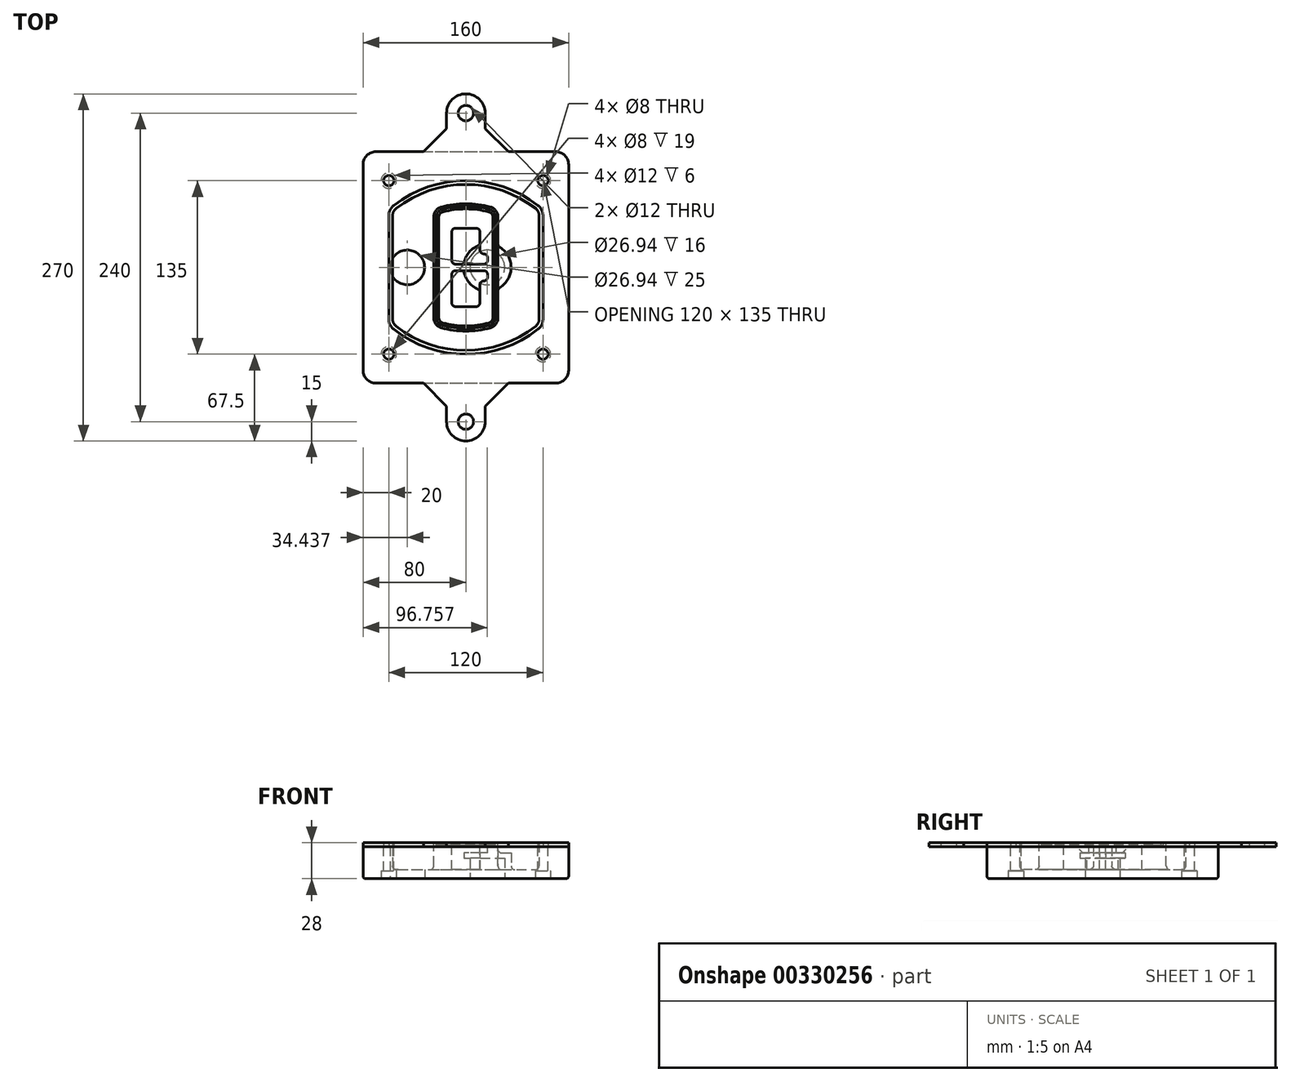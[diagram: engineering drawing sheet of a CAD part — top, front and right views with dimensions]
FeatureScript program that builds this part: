
annotation { "Feature Type Name" : "Feature", "Feature Type Description" : "" }
export const myFeature = defineFeature(function(context is Context, id is Id, definition is map)
    precondition{}
    {
        {
            var Q0;
            Q0=qCreatedBy(makeId("Top.planeOp"),FACE);
            var sketch = newSketch(context, id + "F0", { "sketchPlane" : qUnion([Q0])});
            skPoint(sketch, "E0.rect.middle", {"position": v(0, 0) * mm});
            skLineSegment(sketch, "E1.bottom", {"start": v(-70, -90) * mm, "end": v(70, -90) * mm});
            skLineSegment(sketch, "E1.top", {"start": v(-70, 90) * mm, "end": v(70, 90) * mm});
            skLineSegment(sketch, "E1.left", {"start": v(-80, -80) * mm, "end": v(-80, 80) * mm});
            skLineSegment(sketch, "E1.right", {"start": v(80, -80) * mm, "end": v(80, 80) * mm});
            skLineSegment(sketch, "E2", {"start": v(-80, 90) * mm, "end": v(80, -90) * mm, "construction": true});
            skLineSegment(sketch, "E3", {"start": v(80, 90) * mm, "end": v(-80, -90) * mm, "construction": true});
            skCircle(sketch, "E4", {"center": v(-60, 67.5) * mm, "radius": 4 * mm});
            skCircle(sketch, "E5", {"center": v(60, 67.5) * mm, "radius": 4 * mm});
            skCircle(sketch, "E6", {"center": v(60, -67.5) * mm, "radius": 4 * mm});
            skCircle(sketch, "E7", {"center": v(-60, -67.5) * mm, "radius": 4 * mm});
            skLineSegment(sketch, "E8", {"start": v(-60, 67.5) * mm, "end": v(60, 67.5) * mm, "construction": true});
            skLineSegment(sketch, "E9", {"start": v(60, 67.5) * mm, "end": v(60, -67.5) * mm, "construction": true});
            skLineSegment(sketch, "E10", {"start": v(60, -67.5) * mm, "end": v(-60, -67.5) * mm, "construction": true});
            skLineSegment(sketch, "E11", {"start": v(-60, -67.5) * mm, "end": v(-60, 67.5) * mm, "construction": true});
            skLineSegment(sketch, "E12", {"start": v(-60, 40.3) * mm, "end": v(-60, -40.3) * mm});
            skLineSegment(sketch, "E13", {"start": v(60, 40.3) * mm, "end": v(60, -40.3) * mm});
            skArc(sketch, "E14", {"start": v(56.15, 48.18) * mm, "mid": v(0, 67.5) * mm, "end": v(-56.15, 48.18) * mm});
            skArc(sketch, "E15", {"start": v(-56.15, -48.18) * mm, "mid": v(0, -67.5) * mm, "end": v(56.15, -48.18) * mm});
            skLineSegment(sketch, "E16", {"start": v(-60, 0) * mm, "end": v(60, 0) * mm, "construction": true});
            skPoint(sketch, "E17.visualSharp", {"position": v(-60, -45) * mm});
            skArc(sketch, "E17.filletArc", {"start": v(-60, -40.3) * mm, "mid": v(-58.99, -44.68) * mm, "end": v(-56.15, -48.18) * mm});
            skPoint(sketch, "E18.visualSharp", {"position": v(-60, 45) * mm});
            skArc(sketch, "E18.filletArc", {"start": v(-56.15, 48.18) * mm, "mid": v(-58.99, 44.68) * mm, "end": v(-60, 40.3) * mm});
            skPoint(sketch, "E19.visualSharp", {"position": v(60, 45) * mm});
            skArc(sketch, "E19.filletArc", {"start": v(60, 40.3) * mm, "mid": v(58.99, 44.68) * mm, "end": v(56.15, 48.18) * mm});
            skPoint(sketch, "E20.visualSharp", {"position": v(60, -45) * mm});
            skArc(sketch, "E20.filletArc", {"start": v(56.15, -48.18) * mm, "mid": v(58.99, -44.68) * mm, "end": v(60, -40.3) * mm});
            skPoint(sketch, "E21.visualSharp", {"position": v(-80, 90) * mm});
            skArc(sketch, "E21.filletArc", {"start": v(-70, 90) * mm, "mid": v(-77.07, 87.07) * mm, "end": v(-80, 80) * mm});
            skPoint(sketch, "E22.visualSharp", {"position": v(80, 90) * mm});
            skArc(sketch, "E22.filletArc", {"start": v(80, 80) * mm, "mid": v(77.07, 87.07) * mm, "end": v(70, 90) * mm});
            skPoint(sketch, "E23.visualSharp", {"position": v(80, -90) * mm});
            skArc(sketch, "E23.filletArc", {"start": v(70, -90) * mm, "mid": v(77.07, -87.07) * mm, "end": v(80, -80) * mm});
            skPoint(sketch, "E24.visualSharp", {"position": v(-80, -90) * mm});
            skArc(sketch, "E24.filletArc", {"start": v(-80, -80) * mm, "mid": v(-77.07, -87.07) * mm, "end": v(-70, -90) * mm});
            skArc(sketch, "E25.0", {"start": v(57, 40.3) * mm, "mid": v(56.3, 43.36) * mm, "end": v(54.3, 45.81) * mm});
            skLineSegment(sketch, "E25.1", {"start": v(57, 40.3) * mm, "end": v(57, -40.3) * mm});
            skArc(sketch, "E25.2", {"start": v(54.3, -45.81) * mm, "mid": v(56.3, -43.36) * mm, "end": v(57, -40.3) * mm});
            skArc(sketch, "E25.3", {"start": v(-54.3, -45.81) * mm, "mid": v(0, -64.5) * mm, "end": v(54.3, -45.81) * mm});
            skArc(sketch, "E25.4", {"start": v(-57, -40.3) * mm, "mid": v(-56.3, -43.36) * mm, "end": v(-54.3, -45.81) * mm});
            skArc(sketch, "E25.5", {"start": v(54.3, 45.81) * mm, "mid": v(0, 64.5) * mm, "end": v(-54.3, 45.81) * mm});
            skLineSegment(sketch, "E25.6", {"start": v(-57, 40.3) * mm, "end": v(-57, -40.3) * mm});
            skArc(sketch, "E25.7", {"start": v(-54.3, 45.81) * mm, "mid": v(-56.3, 43.36) * mm, "end": v(-57, 40.3) * mm});
            skArc(sketch, "E26.0", {"start": v(-58.62, 51.33) * mm, "mid": v(-62.58, 46.43) * mm, "end": v(-64, 40.3) * mm});
            skArc(sketch, "E26.1", {"start": v(58.62, 51.33) * mm, "mid": v(0, 71.5) * mm, "end": v(-58.62, 51.33) * mm});
            skArc(sketch, "E26.2", {"start": v(64, 40.3) * mm, "mid": v(62.58, 46.43) * mm, "end": v(58.62, 51.33) * mm});
            skLineSegment(sketch, "E26.3", {"start": v(64, 40.3) * mm, "end": v(64, -40.3) * mm});
            skArc(sketch, "E26.4", {"start": v(58.62, -51.33) * mm, "mid": v(62.58, -46.43) * mm, "end": v(64, -40.3) * mm});
            skLineSegment(sketch, "E26.5", {"start": v(-64, 40.3) * mm, "end": v(-64, -40.3) * mm});
            skArc(sketch, "E26.6", {"start": v(-58.62, -51.33) * mm, "mid": v(0, -71.5) * mm, "end": v(58.62, -51.33) * mm});
            skArc(sketch, "E26.7", {"start": v(-64, -40.3) * mm, "mid": v(-62.58, -46.43) * mm, "end": v(-58.62, -51.33) * mm});
            skSolve(sketch);
        }
        {
            var Q0;
            Q0=makeQuery(id+"F0.imprint","IMPRINT",FACE,{"disambiguationData":[TD([[makeQuery(id+"F0.imprint","IMPRINT",EDGE,{"derivedFrom":sQuery(id+"F0.wireOp",EDGE,"E1.bottom")}),1.0]])]});
            var Q1;
            Q1=makeQuery(id+"F0.imprint","IMPRINT",FACE,{"disambiguationData":[TD([[makeQuery(id+"F0.imprint","IMPRINT",EDGE,{"derivedFrom":sQuery(id+"F0.wireOp",EDGE,"E12")}),1.0]])]});
            var Q2;
            Q2=makeQuery(id+"F0.imprint","IMPRINT",FACE,{"disambiguationData":[TD([[makeQuery(id+"F0.imprint","IMPRINT",EDGE,{"derivedFrom":sQuery(id+"F0.wireOp",EDGE,"E25.0")}),1.0]])]});
            var Q3;
            Q3=makeQuery(id+"F0.imprint","IMPRINT",FACE,{"disambiguationData":[TD([[makeQuery(id+"F0.imprint","IMPRINT",EDGE,{"derivedFrom":sQuery(id+"F0.wireOp",EDGE,"E12")}),-1.0]])]});
            extrude(context, id + "F1", {"entities" : qUnion([Q0, Q1, Q2, Q3]), "oppositeDirection" : true, "depth" : 25 * mm});
        }
        {
            var Q0;
            Q0=makeQuery(id+"F0.imprint","IMPRINT",FACE,{"disambiguationData":[TD([[makeQuery(id+"F0.imprint","IMPRINT",EDGE,{"derivedFrom":sQuery(id+"F0.wireOp",EDGE,"E12")}),1.0]])]});
            extrude(context, id + "F2", {"entities" : qUnion([Q0]), "operationType" : NewBodyOperationType.ADD, "depth" : 3 * mm});
        }
        {
            var Q0;
            Q0=makeQuery(id+"F0.imprint","IMPRINT",FACE,{"disambiguationData":[TD([[makeQuery(id+"F0.imprint","IMPRINT",EDGE,{"derivedFrom":sQuery(id+"F0.wireOp",EDGE,"E25.0")}),1.0]])]});
            extrude(context, id + "F3", {"entities" : qUnion([Q0]), "operationType" : NewBodyOperationType.REMOVE, "oppositeDirection" : true, "depth" : 18 * mm});
        }
        {
            var Q0;
            Q0=makeQuery(id+"F2.opExtrude","CAP_FACE",FACE,{"disambiguationData":[OSD([sQuery(id+"F0.wireOp",EDGE,"E12"),sQuery(id+"F0.wireOp",EDGE,"E13"),sQuery(id+"F0.wireOp",EDGE,"E14"),sQuery(id+"F0.wireOp",EDGE,"E15"),sQuery(id+"F0.wireOp",EDGE,"E17.filletArc"),sQuery(id+"F0.wireOp",EDGE,"E18.filletArc"),sQuery(id+"F0.wireOp",EDGE,"E19.filletArc"),sQuery(id+"F0.wireOp",EDGE,"E20.filletArc"),sQuery(id+"F0.wireOp",EDGE,"E25.0"),sQuery(id+"F0.wireOp",EDGE,"E25.1"),sQuery(id+"F0.wireOp",EDGE,"E25.2"),sQuery(id+"F0.wireOp",EDGE,"E25.3"),sQuery(id+"F0.wireOp",EDGE,"E25.4"),sQuery(id+"F0.wireOp",EDGE,"E25.5"),sQuery(id+"F0.wireOp",EDGE,"E25.6"),sQuery(id+"F0.wireOp",EDGE,"E25.7")])],"isStart":false});
            var sketch = newSketch(context, id + "F4", { "sketchPlane" : qUnion([Q0])});
            skArc(sketch, "E27.0", {"start": v(-19.08, -46.97) * mm, "mid": v(0, -49.5) * mm, "end": v(19.08, -46.97) * mm});
            skArc(sketch, "E28.0", {"start": v(19.08, 46.97) * mm, "mid": v(0, 49.5) * mm, "end": v(-19.08, 46.97) * mm});
            skLineSegment(sketch, "E29", {"start": v(-25, 39.25) * mm, "end": v(-25, -39.25) * mm});
            skLineSegment(sketch, "E30", {"start": v(25, 39.25) * mm, "end": v(25, -39.25) * mm});
            skLineSegment(sketch, "E31", {"start": v(-25, 45.1) * mm, "end": v(25, 45.1) * mm, "construction": true});
            skLineSegment(sketch, "E32", {"start": v(-25, -45.1) * mm, "end": v(25, -45.1) * mm, "construction": true});
            skPoint(sketch, "E33.visualSharp", {"position": v(-25, 45.1) * mm});
            skArc(sketch, "E33.filletArc", {"start": v(-19.08, 46.97) * mm, "mid": v(-23.35, 44.11) * mm, "end": v(-25, 39.25) * mm});
            skPoint(sketch, "E34.visualSharp", {"position": v(25, 45.1) * mm});
            skArc(sketch, "E34.filletArc", {"start": v(25, 39.25) * mm, "mid": v(23.35, 44.11) * mm, "end": v(19.08, 46.97) * mm});
            skPoint(sketch, "E35.visualSharp", {"position": v(25, -45.1) * mm});
            skArc(sketch, "E35.filletArc", {"start": v(19.08, -46.97) * mm, "mid": v(23.35, -44.11) * mm, "end": v(25, -39.25) * mm});
            skPoint(sketch, "E36.visualSharp", {"position": v(-25, -45.1) * mm});
            skArc(sketch, "E36.filletArc", {"start": v(-25, -39.25) * mm, "mid": v(-23.35, -44.11) * mm, "end": v(-19.08, -46.97) * mm});
            skArc(sketch, "E37.0", {"start": v(54.3, 45.81) * mm, "mid": v(0, 64.5) * mm, "end": v(-54.3, 45.81) * mm});
            skArc(sketch, "E37.1", {"start": v(-54.3, 45.81) * mm, "mid": v(-56.3, 43.36) * mm, "end": v(-57, 40.3) * mm});
            skLineSegment(sketch, "E37.2", {"start": v(-57, 40.3) * mm, "end": v(-57, -40.3) * mm});
            skArc(sketch, "E37.3", {"start": v(-57, -40.3) * mm, "mid": v(-56.3, -43.36) * mm, "end": v(-54.3, -45.81) * mm});
            skArc(sketch, "E37.4", {"start": v(-54.3, -45.81) * mm, "mid": v(0, -64.5) * mm, "end": v(54.3, -45.81) * mm});
            skArc(sketch, "E37.5", {"start": v(54.3, -45.81) * mm, "mid": v(56.3, -43.36) * mm, "end": v(57, -40.3) * mm});
            skLineSegment(sketch, "E37.6", {"start": v(57, 40.3) * mm, "end": v(57, -40.3) * mm});
            skArc(sketch, "E37.7", {"start": v(57, 40.3) * mm, "mid": v(56.3, 43.36) * mm, "end": v(54.3, 45.81) * mm});
            skLineSegment(sketch, "E38.0", {"start": v(23, 39.25) * mm, "end": v(23, -39.25) * mm});
            skArc(sketch, "E38.1", {"start": v(18.56, -45.04) * mm, "mid": v(21.76, -42.9) * mm, "end": v(23, -39.25) * mm});
            skArc(sketch, "E38.2", {"start": v(-18.56, -45.04) * mm, "mid": v(0, -47.5) * mm, "end": v(18.56, -45.04) * mm});
            skArc(sketch, "E38.3", {"start": v(-23, -39.25) * mm, "mid": v(-21.76, -42.9) * mm, "end": v(-18.56, -45.04) * mm});
            skLineSegment(sketch, "E38.4", {"start": v(-23, 39.25) * mm, "end": v(-23, -39.25) * mm});
            skArc(sketch, "E38.5", {"start": v(23, 39.25) * mm, "mid": v(21.76, 42.9) * mm, "end": v(18.56, 45.04) * mm});
            skArc(sketch, "E38.6", {"start": v(-18.56, 45.04) * mm, "mid": v(-21.76, 42.9) * mm, "end": v(-23, 39.25) * mm});
            skArc(sketch, "E38.7", {"start": v(18.56, 45.04) * mm, "mid": v(0, 47.5) * mm, "end": v(-18.56, 45.04) * mm});
            skArc(sketch, "E39.0", {"start": v(21, 39.25) * mm, "mid": v(20.18, 41.68) * mm, "end": v(18.04, 43.1) * mm});
            skLineSegment(sketch, "E39.1", {"start": v(21, 39.25) * mm, "end": v(21, -39.25) * mm});
            skArc(sketch, "E39.2", {"start": v(18.04, -43.1) * mm, "mid": v(20.18, -41.68) * mm, "end": v(21, -39.25) * mm});
            skArc(sketch, "E39.3", {"start": v(-18.04, -43.1) * mm, "mid": v(0, -45.5) * mm, "end": v(18.04, -43.1) * mm});
            skArc(sketch, "E39.4", {"start": v(-21, -39.25) * mm, "mid": v(-20.18, -41.68) * mm, "end": v(-18.04, -43.1) * mm});
            skArc(sketch, "E39.5", {"start": v(18.04, 43.1) * mm, "mid": v(0, 45.5) * mm, "end": v(-18.04, 43.1) * mm});
            skLineSegment(sketch, "E39.6", {"start": v(-21, 39.25) * mm, "end": v(-21, -39.25) * mm});
            skArc(sketch, "E39.7", {"start": v(-18.04, 43.1) * mm, "mid": v(-20.18, 41.68) * mm, "end": v(-21, 39.25) * mm});
            skLineSegment(sketch, "E40", {"start": v(-25, 0) * mm, "end": v(25, 0) * mm, "construction": true});
            skLineSegment(sketch, "E41", {"start": v(-11, 5.5) * mm, "end": v(-11, 27.5) * mm});
            skLineSegment(sketch, "E42", {"start": v(-8, 30.5) * mm, "end": v(8, 30.5) * mm});
            skLineSegment(sketch, "E43", {"start": v(11, 27.5) * mm, "end": v(11, 13.5) * mm});
            skLineSegment(sketch, "E44", {"start": v(14, 10.5) * mm, "end": v(14, 10.5) * mm});
            skLineSegment(sketch, "E45", {"start": v(17, 7.5) * mm, "end": v(17, 5.5) * mm});
            skLineSegment(sketch, "E46", {"start": v(14, 2.5) * mm, "end": v(-8, 2.5) * mm});
            skPoint(sketch, "E47.visualSharp", {"position": v(-11, 30.5) * mm});
            skArc(sketch, "E47.filletArc", {"start": v(-8, 30.5) * mm, "mid": v(-10.12, 29.62) * mm, "end": v(-11, 27.5) * mm});
            skPoint(sketch, "E48.visualSharp", {"position": v(11, 30.5) * mm});
            skArc(sketch, "E48.filletArc", {"start": v(11, 27.5) * mm, "mid": v(10.12, 29.62) * mm, "end": v(8, 30.5) * mm});
            skPoint(sketch, "E49.visualSharp", {"position": v(11, 10.5) * mm});
            skArc(sketch, "E49.filletArc", {"start": v(11, 13.5) * mm, "mid": v(11.88, 11.38) * mm, "end": v(14, 10.5) * mm});
            skPoint(sketch, "E50.visualSharp", {"position": v(17, 10.5) * mm});
            skArc(sketch, "E50.filletArc", {"start": v(17, 7.5) * mm, "mid": v(16.12, 9.62) * mm, "end": v(14, 10.5) * mm});
            skPoint(sketch, "E51.visualSharp", {"position": v(17, 2.5) * mm});
            skArc(sketch, "E51.filletArc", {"start": v(14, 2.5) * mm, "mid": v(16.12, 3.38) * mm, "end": v(17, 5.5) * mm});
            skPoint(sketch, "E52.visualSharp", {"position": v(-11, 2.5) * mm});
            skArc(sketch, "E52.filletArc", {"start": v(-11, 5.5) * mm, "mid": v(-10.12, 3.38) * mm, "end": v(-8, 2.5) * mm});
            skLineSegment(sketch, "E53.0.MirrorCS", {"start": v(14, -2.5) * mm, "end": v(-8, -2.5) * mm});
            skArc(sketch, "E54.0.MirrorCS", {"start": v(-11, -5.5) * mm, "mid": v(-10.12, -3.38) * mm, "end": v(-8, -2.5) * mm});
            skLineSegment(sketch, "E55.0.MirrorCS", {"start": v(-11, -5.5) * mm, "end": v(-11, -27.5) * mm});
            skArc(sketch, "E56.0.MirrorCS", {"start": v(-8, -30.5) * mm, "mid": v(-10.12, -29.62) * mm, "end": v(-11, -27.5) * mm});
            skLineSegment(sketch, "E57.0.MirrorCS", {"start": v(-8, -30.5) * mm, "end": v(8, -30.5) * mm});
            skArc(sketch, "E58.0.MirrorCS", {"start": v(11, -27.5) * mm, "mid": v(10.12, -29.62) * mm, "end": v(8, -30.5) * mm});
            skLineSegment(sketch, "E59.0.MirrorCS", {"start": v(11, -27.5) * mm, "end": v(11, -13.5) * mm});
            skArc(sketch, "E60.0.MirrorCS", {"start": v(11, -13.5) * mm, "mid": v(11.88, -11.38) * mm, "end": v(14, -10.5) * mm});
            skArc(sketch, "E61.0.MirrorCS", {"start": v(17, -7.5) * mm, "mid": v(16.12, -9.62) * mm, "end": v(14, -10.5) * mm});
            skLineSegment(sketch, "E62.0.MirrorCS", {"start": v(17, -7.5) * mm, "end": v(17, -5.5) * mm});
            skArc(sketch, "E63.0.MirrorCS", {"start": v(14, -2.5) * mm, "mid": v(16.12, -3.38) * mm, "end": v(17, -5.5) * mm});
            skSolve(sketch);
        }
        {
            var Q0;
            Q0=makeQuery(id+"F4.imprint","IMPRINT",FACE,{"disambiguationData":[TD([[makeQuery(id+"F4.imprint","IMPRINT",EDGE,{"derivedFrom":sQuery(id+"F4.wireOp",EDGE,"E27.0")}),1.0]])]});
            var Q1;
            Q1=makeQuery(id+"F4.imprint","IMPRINT",FACE,{"disambiguationData":[TD([[makeQuery(id+"F4.imprint","IMPRINT",EDGE,{"derivedFrom":sQuery(id+"F4.wireOp",EDGE,"E38.0")}),-1.0]])]});
            var Q2;
            Q2=makeQuery(id+"F4.imprint","IMPRINT",FACE,{"disambiguationData":[TD([[makeQuery(id+"F4.imprint","IMPRINT",EDGE,{"derivedFrom":sQuery(id+"F4.wireOp",EDGE,"E39.0")}),1.0]])]});
            extrude(context, id + "F5", {"entities" : qUnion([Q0, Q1, Q2]), "operationType" : NewBodyOperationType.ADD, "endBound" : BoundingType.UP_TO_NEXT, "oppositeDirection" : true, "depth" : 25 * mm});
        }
        {
            var Q0;
            Q0=makeQuery(id+"F4.imprint","IMPRINT",FACE,{"disambiguationData":[TD([[makeQuery(id+"F4.imprint","IMPRINT",EDGE,{"derivedFrom":sQuery(id+"F4.wireOp",EDGE,"E38.0")}),-1.0]])]});
            extrude(context, id + "F6", {"entities" : qUnion([Q0]), "operationType" : NewBodyOperationType.REMOVE, "oppositeDirection" : true, "depth" : 2 * mm});
        }
        {
            var Q0;
            Q0=makeQuery(id+"F1.opExtrude","CAP_FACE",FACE,{"disambiguationData":[OSD([sQuery(id+"F0.wireOp",EDGE,"E1.bottom"),sQuery(id+"F0.wireOp",EDGE,"E1.top"),sQuery(id+"F0.wireOp",EDGE,"E1.left"),sQuery(id+"F0.wireOp",EDGE,"E1.right"),sQuery(id+"F0.wireOp",EDGE,"E4"),sQuery(id+"F0.wireOp",EDGE,"E5"),sQuery(id+"F0.wireOp",EDGE,"E6"),sQuery(id+"F0.wireOp",EDGE,"E7"),sQuery(id+"F0.wireOp",EDGE,"E21.filletArc"),sQuery(id+"F0.wireOp",EDGE,"E22.filletArc"),sQuery(id+"F0.wireOp",EDGE,"E23.filletArc"),sQuery(id+"F0.wireOp",EDGE,"E24.filletArc")])],"isStart":false});
            var sketch = newSketch(context, id + "F7", { "sketchPlane" : qUnion([Q0])});
            skCircle(sketch, "E64", {"center": v(16.76, 0) * mm, "radius": 13.47 * mm});
            skCircle(sketch, "E65", {"center": v(-45.56, 0) * mm, "radius": 13.47 * mm});
            skLineSegment(sketch, "E66", {"start": v(80, 0) * mm, "end": v(-80, 0) * mm});
            skCircle(sketch, "E67", {"center": v(16.76, 0) * mm, "radius": 18.47 * mm});
            skCircle(sketch, "E68", {"center": v(60, -67.5) * mm, "radius": 6 * mm});
            skCircle(sketch, "E69", {"center": v(-60, -67.5) * mm, "radius": 6 * mm});
            skCircle(sketch, "E70", {"center": v(-60, 67.5) * mm, "radius": 6 * mm});
            skCircle(sketch, "E71", {"center": v(60, 67.5) * mm, "radius": 6 * mm});
            skSolve(sketch);
        }
        {
            var Q0;
            {var subQ1=sQuery(id+"F7.wireOp",EDGE,"E66");var subQ4=sQuery(id+"F7.wireOp",EDGE,"E64");var subQ6=makeQuery(id+"F7.imprint","INTERSECT",VERTEX,{"disambiguationData":[OD(0.0)],"derivedFrom":[subQ4,subQ1]});Q0=makeQuery(id+"F7.imprint","IMPRINT",FACE,{"disambiguationData":[TD([[makeQuery(id+"F7.imprint","IMPRINT",EDGE,{"disambiguationData":[TD([[subQ6,-1.0]])],"derivedFrom":subQ4}),-1.0]])]});}
            var Q1;
            {var subQ0=sQuery(id+"F7.wireOp",EDGE,"E66");var subQ1=sQuery(id+"F7.wireOp",EDGE,"E64");var subQ3=makeQuery(id+"F7.imprint","INTERSECT",VERTEX,{"disambiguationData":[OD(0.0)],"derivedFrom":[subQ1,subQ0]});Q1=makeQuery(id+"F7.imprint","IMPRINT",FACE,{"disambiguationData":[TD([[makeQuery(id+"F7.imprint","IMPRINT",EDGE,{"disambiguationData":[TD([[subQ3,-1.0]])],"derivedFrom":subQ1}),1.0]])]});}
            var Q2;
            {var subQ0=sQuery(id+"F7.wireOp",EDGE,"E66");var subQ1=sQuery(id+"F7.wireOp",EDGE,"E64");var subQ3=makeQuery(id+"F7.imprint","INTERSECT",VERTEX,{"disambiguationData":[OD(0.0)],"derivedFrom":[subQ1,subQ0]});Q2=makeQuery(id+"F7.imprint","IMPRINT",FACE,{"disambiguationData":[TD([[makeQuery(id+"F7.imprint","IMPRINT",EDGE,{"disambiguationData":[TD([[subQ3,1.0]])],"derivedFrom":subQ1}),1.0]])]});}
            var Q3;
            {var subQ1=sQuery(id+"F7.wireOp",EDGE,"E66");var subQ4=sQuery(id+"F7.wireOp",EDGE,"E64");var subQ6=makeQuery(id+"F7.imprint","INTERSECT",VERTEX,{"disambiguationData":[OD(0.0)],"derivedFrom":[subQ4,subQ1]});Q3=makeQuery(id+"F7.imprint","IMPRINT",FACE,{"disambiguationData":[TD([[makeQuery(id+"F7.imprint","IMPRINT",EDGE,{"disambiguationData":[TD([[subQ6,1.0]])],"derivedFrom":subQ4}),-1.0]])]});}
            extrude(context, id + "F8", {"entities" : qUnion([Q0, Q1, Q2, Q3]), "operationType" : NewBodyOperationType.ADD, "oppositeDirection" : true, "depth" : 20 * mm});
        }
        {
            var Q0;
            {var subQ0=sQuery(id+"F7.wireOp",EDGE,"E66");var subQ1=sQuery(id+"F7.wireOp",EDGE,"E64");var subQ3=makeQuery(id+"F7.imprint","INTERSECT",VERTEX,{"disambiguationData":[OD(0.0)],"derivedFrom":[subQ1,subQ0]});Q0=makeQuery(id+"F7.imprint","IMPRINT",FACE,{"disambiguationData":[TD([[makeQuery(id+"F7.imprint","IMPRINT",EDGE,{"disambiguationData":[TD([[subQ3,-1.0]])],"derivedFrom":subQ1}),1.0]])]});}
            var Q1;
            {var subQ0=sQuery(id+"F7.wireOp",EDGE,"E66");var subQ1=sQuery(id+"F7.wireOp",EDGE,"E64");var subQ3=makeQuery(id+"F7.imprint","INTERSECT",VERTEX,{"disambiguationData":[OD(0.0)],"derivedFrom":[subQ1,subQ0]});Q1=makeQuery(id+"F7.imprint","IMPRINT",FACE,{"disambiguationData":[TD([[makeQuery(id+"F7.imprint","IMPRINT",EDGE,{"disambiguationData":[TD([[subQ3,1.0]])],"derivedFrom":subQ1}),1.0]])]});}
            extrude(context, id + "F9", {"entities" : qUnion([Q0, Q1]), "operationType" : NewBodyOperationType.REMOVE, "oppositeDirection" : true, "depth" : 16 * mm});
        }
        {
            var Q0;
            {var subQ0=sQuery(id+"F7.wireOp",EDGE,"E66");var subQ1=sQuery(id+"F7.wireOp",EDGE,"E65");var subQ3=makeQuery(id+"F7.imprint","INTERSECT",VERTEX,{"disambiguationData":[OD(0.0)],"derivedFrom":[subQ1,subQ0]});Q0=makeQuery(id+"F7.imprint","IMPRINT",FACE,{"disambiguationData":[TD([[makeQuery(id+"F7.imprint","IMPRINT",EDGE,{"disambiguationData":[TD([[subQ3,-1.0]])],"derivedFrom":subQ1}),1.0]])]});}
            var Q1;
            {var subQ0=sQuery(id+"F7.wireOp",EDGE,"E66");var subQ1=sQuery(id+"F7.wireOp",EDGE,"E65");var subQ3=makeQuery(id+"F7.imprint","INTERSECT",VERTEX,{"disambiguationData":[OD(0.0)],"derivedFrom":[subQ1,subQ0]});Q1=makeQuery(id+"F7.imprint","IMPRINT",FACE,{"disambiguationData":[TD([[makeQuery(id+"F7.imprint","IMPRINT",EDGE,{"disambiguationData":[TD([[subQ3,1.0]])],"derivedFrom":subQ1}),1.0]])]});}
            extrude(context, id + "F10", {"entities" : qUnion([Q0, Q1]), "operationType" : NewBodyOperationType.REMOVE, "oppositeDirection" : true, "depth" : 25 * mm});
        }
        {
            var Q0;
            Q0=makeQuery(id+"F7.imprint","IMPRINT",FACE,{"disambiguationData":[TD([[makeQuery(id+"F7.imprint","IMPRINT",EDGE,{"derivedFrom":sQuery(id+"F7.wireOp",EDGE,"E68")}),1.0]])]});
            var Q1;
            Q1=makeQuery(id+"F7.imprint","IMPRINT",FACE,{"disambiguationData":[TD([[makeQuery(id+"F7.imprint","IMPRINT",EDGE,{"derivedFrom":makeQuery(id+"F1.opExtrude","CAP_EDGE",EDGE,{"disambiguationData":[OSD([sQuery(id+"F0.wireOp",EDGE,"E5")])],"isStart":false})}),-1.0]])]});
            var Q2;
            Q2=makeQuery(id+"F7.imprint","IMPRINT",FACE,{"disambiguationData":[TD([[makeQuery(id+"F7.imprint","IMPRINT",EDGE,{"derivedFrom":sQuery(id+"F7.wireOp",EDGE,"E69")}),1.0]])]});
            var Q3;
            Q3=makeQuery(id+"F7.imprint","IMPRINT",FACE,{"disambiguationData":[TD([[makeQuery(id+"F7.imprint","IMPRINT",EDGE,{"derivedFrom":makeQuery(id+"F1.opExtrude","CAP_EDGE",EDGE,{"disambiguationData":[OSD([sQuery(id+"F0.wireOp",EDGE,"E4")])],"isStart":false})}),-1.0]])]});
            var Q4;
            Q4=makeQuery(id+"F7.imprint","IMPRINT",FACE,{"disambiguationData":[TD([[makeQuery(id+"F7.imprint","IMPRINT",EDGE,{"derivedFrom":sQuery(id+"F7.wireOp",EDGE,"E70")}),1.0]])]});
            var Q5;
            Q5=makeQuery(id+"F7.imprint","IMPRINT",FACE,{"disambiguationData":[TD([[makeQuery(id+"F7.imprint","IMPRINT",EDGE,{"derivedFrom":makeQuery(id+"F1.opExtrude","CAP_EDGE",EDGE,{"disambiguationData":[OSD([sQuery(id+"F0.wireOp",EDGE,"E7")])],"isStart":false})}),-1.0]])]});
            var Q6;
            Q6=makeQuery(id+"F7.imprint","IMPRINT",FACE,{"disambiguationData":[TD([[makeQuery(id+"F7.imprint","IMPRINT",EDGE,{"derivedFrom":sQuery(id+"F7.wireOp",EDGE,"E71")}),1.0]])]});
            var Q7;
            Q7=makeQuery(id+"F7.imprint","IMPRINT",FACE,{"disambiguationData":[TD([[makeQuery(id+"F7.imprint","IMPRINT",EDGE,{"derivedFrom":makeQuery(id+"F1.opExtrude","CAP_EDGE",EDGE,{"disambiguationData":[OSD([sQuery(id+"F0.wireOp",EDGE,"E6")])],"isStart":false})}),-1.0]])]});
            extrude(context, id + "F11", {"entities" : qUnion([Q0, Q1, Q2, Q3, Q4, Q5, Q6, Q7]), "operationType" : NewBodyOperationType.REMOVE, "oppositeDirection" : true, "depth" : 6 * mm});
        }
        {
            var Q0;
            Q0=makeQuery(id+"F9.boolean.opBoolean","COPY",FACE,{"derivedFrom":makeQuery(id+"F9.opExtrude","CAP_FACE",FACE,{"disambiguationData":[OSD([sQuery(id+"F7.wireOp",EDGE,"E64")])],"isStart":false})});
            var sketch = newSketch(context, id + "F12", { "sketchPlane" : qUnion([Q0])});
            skArc(sketch, "E72.0", {"start": v(11, 17.55) * mm, "mid": v(2.57, 11.82) * mm, "end": v(-1.54, 2.5) * mm});
            skArc(sketch, "E72.1", {"start": v(-1.54, -2.5) * mm, "mid": v(2.57, -11.82) * mm, "end": v(11, -17.55) * mm});
            skLineSegment(sketch, "E73", {"start": v(-1.54, -2.5) * mm, "end": v(14, -2.5) * mm});
            skLineSegment(sketch, "E74.0", {"start": v(14, 2.5) * mm, "end": v(-1.54, 2.5) * mm});
            skArc(sketch, "E74.1", {"start": v(14, 2.5) * mm, "mid": v(16.12, 3.38) * mm, "end": v(17, 5.5) * mm});
            skLineSegment(sketch, "E74.2", {"start": v(17, 7.5) * mm, "end": v(17, 5.5) * mm});
            skArc(sketch, "E74.3", {"start": v(17, 7.5) * mm, "mid": v(16.12, 9.62) * mm, "end": v(14, 10.5) * mm});
            skArc(sketch, "E74.4", {"start": v(11, 13.5) * mm, "mid": v(11.88, 11.38) * mm, "end": v(14, 10.5) * mm});
            skLineSegment(sketch, "E74.5", {"start": v(11, 17.55) * mm, "end": v(11, 13.5) * mm});
            skLineSegment(sketch, "E74.7", {"start": v(14, -2.5) * mm, "end": v(-1.54, -2.5) * mm});
            skArc(sketch, "E74.8", {"start": v(14, -2.5) * mm, "mid": v(16.12, -3.38) * mm, "end": v(17, -5.5) * mm});
            skLineSegment(sketch, "E74.9", {"start": v(17, -7.5) * mm, "end": v(17, -5.5) * mm});
            skArc(sketch, "E74.10", {"start": v(17, -7.5) * mm, "mid": v(16.12, -9.62) * mm, "end": v(14, -10.5) * mm});
            skArc(sketch, "E74.11", {"start": v(11, -13.5) * mm, "mid": v(11.88, -11.38) * mm, "end": v(14, -10.5) * mm});
            skLineSegment(sketch, "E74.12", {"start": v(11, -17.55) * mm, "end": v(11, -13.5) * mm});
            skPoint(sketch, "E75.orphan", {"position": v(11, -27.5) * mm});
            skPoint(sketch, "E76.orphan", {"position": v(-8, -2.5) * mm});
            skPoint(sketch, "E77.orphan", {"position": v(-8, 2.5) * mm});
            skPoint(sketch, "E78.orphan", {"position": v(11, 27.5) * mm});
            skSolve(sketch);
        }
        {
            var Q0;
            {var subQ7=sQuery(id+"F12.wireOp",EDGE,"E72.0");var subQ14=sQuery(id+"F12.wireOp",EDGE,"E72.1");var subQ16=sQuery(id+"F12.wireOp",EDGE,"E74.1");var subQ18=sQuery(id+"F12.wireOp",EDGE,"E74.8");Q0=qUnion([makeQuery(id+"F12.imprint","IMPRINT",FACE,{"disambiguationData":[TD([[makeQuery(id+"F12.imprint","IMPRINT",EDGE,{"derivedFrom":subQ7}),1.0]])]}),makeQuery(id+"F12.imprint","IMPRINT",FACE,{"disambiguationData":[TD([[makeQuery(id+"F12.imprint","IMPRINT",EDGE,{"derivedFrom":subQ14}),1.0]])]}),makeQuery(id+"F12.imprint","IMPRINT",FACE,{"disambiguationData":[TD([[makeQuery(id+"F12.imprint","IMPRINT",EDGE,{"derivedFrom":subQ16}),1.0]])]}),makeQuery(id+"F12.imprint","IMPRINT",FACE,{"disambiguationData":[TD([[makeQuery(id+"F12.imprint","IMPRINT",EDGE,{"derivedFrom":subQ18}),-1.0]])]})]);}
            var Q1;
            Q1=makeQuery(id+"F5.boolean.opBoolean","SPLIT",FACE,{"disambiguationData":[TD([makeQuery(id+"F5.opExtrude","SWEPT_FACE",FACE,{"disambiguationData":[OSD([sQuery(id+"F4.wireOp",EDGE,"E41")])]})])],"derivedFrom":makeQuery(id+"F3.boolean.opBoolean","COPY",FACE,{"derivedFrom":makeQuery(id+"F3.opExtrude","CAP_FACE",FACE,{"disambiguationData":[OSD([sQuery(id+"F0.wireOp",EDGE,"E25.0"),sQuery(id+"F0.wireOp",EDGE,"E25.1"),sQuery(id+"F0.wireOp",EDGE,"E25.2"),sQuery(id+"F0.wireOp",EDGE,"E25.3"),sQuery(id+"F0.wireOp",EDGE,"E25.4"),sQuery(id+"F0.wireOp",EDGE,"E25.5"),sQuery(id+"F0.wireOp",EDGE,"E25.6"),sQuery(id+"F0.wireOp",EDGE,"E25.7")])],"isStart":false})})});
            extrude(context, id + "F13", {"entities" : qUnion([Q0]), "operationType" : NewBodyOperationType.REMOVE, "endBound" : BoundingType.UP_TO_SURFACE, "endBoundEntityFace" : qUnion([Q1]), "depth" : 25 * mm});
        }
        {
            var Q0;
            Q0=makeQuery(id+"F3.boolean.opBoolean","COPY",EDGE,{"derivedFrom":makeQuery(id+"F3.opExtrude","CAP_EDGE",EDGE,{"disambiguationData":[OSD([sQuery(id+"F0.wireOp",EDGE,"E25.6")])],"isStart":false})});
            var Q1;
            Q1=makeQuery(id+"F8.boolean.opBoolean","INTERSECT",EDGE,{"derivedFrom":[makeQuery(id+"F5.opExtrude","SWEPT_FACE",FACE,{"disambiguationData":[OSD([sQuery(id+"F4.wireOp",EDGE,"E30")])]}),makeQuery(id+"F8.opExtrude","CAP_FACE",FACE,{"disambiguationData":[OSD([sQuery(id+"F7.wireOp",EDGE,"E67")])],"isStart":false})]});
            var Q2;
            Q2=makeQuery(id+"F8.boolean.opBoolean","INTERSECT",EDGE,{"disambiguationData":[OD(1.0)],"derivedFrom":[makeQuery(id+"F5.opExtrude","SWEPT_FACE",FACE,{"disambiguationData":[OSD([sQuery(id+"F4.wireOp",EDGE,"E30")])]}),makeQuery(id+"F8.opExtrude","SWEPT_FACE",FACE,{"disambiguationData":[OSD([sQuery(id+"F7.wireOp",EDGE,"E67")])]})]});
            var Q3;
            {var subQ0=sQuery(id+"F4.wireOp",EDGE,"E30");Q3=makeQuery(id+"F8.boolean.opBoolean","SPLIT",EDGE,{"disambiguationData":[TD([makeQuery(id+"F5.opExtrude","SWEPT_FACE",FACE,{"disambiguationData":[OSD([sQuery(id+"F4.wireOp",EDGE,"E35.filletArc")])]})])],"derivedFrom":makeQuery(id+"F5.opExtrude","CAP_EDGE",EDGE,{"disambiguationData":[OSD([subQ0])],"isStart":false})});}
            var Q4;
            {var subQ0=sQuery(id+"F0.wireOp",EDGE,"E25.7");var subQ1=sQuery(id+"F0.wireOp",EDGE,"E25.1");var subQ2=sQuery(id+"F0.wireOp",EDGE,"E25.6");var subQ3=sQuery(id+"F0.wireOp",EDGE,"E25.5");var subQ4=sQuery(id+"F0.wireOp",EDGE,"E25.4");var subQ5=sQuery(id+"F0.wireOp",EDGE,"E25.0");var subQ6=sQuery(id+"F0.wireOp",EDGE,"E25.2");var subQ7=sQuery(id+"F0.wireOp",EDGE,"E25.3");Q4=makeQuery(id+"F8.boolean.opBoolean","INTERSECT",EDGE,{"derivedFrom":[makeQuery(id+"F5.boolean.opBoolean","SPLIT",FACE,{"disambiguationData":[TD([makeQuery(id+"F2.opExtrude","SWEPT_FACE",FACE,{"disambiguationData":[OSD([subQ5])]})])],"derivedFrom":makeQuery(id+"F3.boolean.opBoolean","COPY",FACE,{"derivedFrom":makeQuery(id+"F3.opExtrude","CAP_FACE",FACE,{"disambiguationData":[OSD([subQ5,subQ1,subQ6,subQ7,subQ4,subQ3,subQ2,subQ0])],"isStart":false})})}),makeQuery(id+"F8.opExtrude","SWEPT_FACE",FACE,{"disambiguationData":[OSD([sQuery(id+"F7.wireOp",EDGE,"E67")])]})]});}
            var Q5;
            Q5=makeQuery(id+"F8.boolean.opBoolean","INTERSECT",EDGE,{"disambiguationData":[OD(0.0)],"derivedFrom":[makeQuery(id+"F5.opExtrude","SWEPT_FACE",FACE,{"disambiguationData":[OSD([sQuery(id+"F4.wireOp",EDGE,"E30")])]}),makeQuery(id+"F8.opExtrude","SWEPT_FACE",FACE,{"disambiguationData":[OSD([sQuery(id+"F7.wireOp",EDGE,"E67")])]})]});
            fillet(context, id + "F14", {"entities" : qUnion([Q0, Q1, Q2, Q3, Q4, Q5]), "radius" : 3 * mm, "tangentPropagation" : true, "allowEdgeOverflow" : false});
        }
        {
            var Q0;
            Q0=makeQuery(id+"F1.opExtrude","CAP_EDGE",EDGE,{"disambiguationData":[OSD([sQuery(id+"F0.wireOp",EDGE,"E1.bottom")])],"isStart":false});
            fillet(context, id + "F15", {"entities" : qUnion([Q0]), "radius" : 2 * mm, "tangentPropagation" : true, "allowEdgeOverflow" : false});
        }
        {
            var Q0;
            {var subQ0=sQuery(id+"F0.wireOp",EDGE,"E21.filletArc");var subQ1=sQuery(id+"F0.wireOp",EDGE,"E7");var subQ2=sQuery(id+"F0.wireOp",EDGE,"E6");var subQ3=sQuery(id+"F0.wireOp",EDGE,"E5");var subQ4=sQuery(id+"F0.wireOp",EDGE,"E4");var subQ5=sQuery(id+"F0.wireOp",EDGE,"E22.filletArc");var subQ6=sQuery(id+"F0.wireOp",EDGE,"E1.bottom");var subQ7=sQuery(id+"F0.wireOp",EDGE,"E1.right");var subQ8=sQuery(id+"F0.wireOp",EDGE,"E1.top");var subQ9=sQuery(id+"F0.wireOp",EDGE,"E1.left");var subQ10=sQuery(id+"F0.wireOp",EDGE,"E23.filletArc");var subQ11=sQuery(id+"F0.wireOp",EDGE,"E24.filletArc");Q0=makeQuery(id+"F2.boolean.opBoolean","SPLIT",FACE,{"disambiguationData":[TD([makeQuery(id+"F1.opExtrude","SWEPT_FACE",FACE,{"disambiguationData":[OSD([subQ6])]})])],"derivedFrom":makeQuery(id+"F1.opExtrude","CAP_FACE",FACE,{"disambiguationData":[OSD([subQ6,subQ8,subQ9,subQ7,subQ4,subQ3,subQ2,subQ1,subQ0,subQ5,subQ10,subQ11])],"isStart":true})});}
            var sketch = newSketch(context, id + "F16", { "sketchPlane" : qUnion([Q0])});
            skLineSegment(sketch, "E79.0", {"start": v(-70, 90) * mm, "end": v(70, 90) * mm});
            skArc(sketch, "E79.1", {"start": v(-70, 90) * mm, "mid": v(-77.07, 87.07) * mm, "end": v(-80, 80) * mm});
            skLineSegment(sketch, "E79.2", {"start": v(-80, -80) * mm, "end": v(-80, 80) * mm});
            skArc(sketch, "E79.3", {"start": v(-80, -80) * mm, "mid": v(-77.07, -87.07) * mm, "end": v(-70, -90) * mm});
            skLineSegment(sketch, "E80.0", {"start": v(-70, -90) * mm, "end": v(70, -90) * mm});
            skArc(sketch, "E80.1", {"start": v(70, -90) * mm, "mid": v(77.07, -87.07) * mm, "end": v(80, -80) * mm});
            skLineSegment(sketch, "E80.2", {"start": v(80, -80) * mm, "end": v(80, 80) * mm});
            skArc(sketch, "E80.3", {"start": v(80, 80) * mm, "mid": v(77.07, 87.07) * mm, "end": v(70, 90) * mm});
            skLineSegment(sketch, "E81.0", {"start": v(60, 40.3) * mm, "end": v(60, -40.3) * mm});
            skArc(sketch, "E81.1", {"start": v(60, 40.3) * mm, "mid": v(58.99, 44.68) * mm, "end": v(56.15, 48.18) * mm});
            skArc(sketch, "E81.2", {"start": v(56.15, 48.18) * mm, "mid": v(0, 67.5) * mm, "end": v(-56.15, 48.18) * mm});
            skArc(sketch, "E81.3", {"start": v(-56.15, 48.18) * mm, "mid": v(-58.99, 44.68) * mm, "end": v(-60, 40.3) * mm});
            skLineSegment(sketch, "E81.4", {"start": v(-60, 40.3) * mm, "end": v(-60, -40.3) * mm});
            skArc(sketch, "E81.5", {"start": v(-60, -40.3) * mm, "mid": v(-58.99, -44.68) * mm, "end": v(-56.15, -48.18) * mm});
            skArc(sketch, "E81.6", {"start": v(-56.15, -48.18) * mm, "mid": v(0, -67.5) * mm, "end": v(56.15, -48.18) * mm});
            skArc(sketch, "E81.7", {"start": v(56.15, -48.18) * mm, "mid": v(58.99, -44.68) * mm, "end": v(60, -40.3) * mm});
            skCircle(sketch, "E82.0", {"center": v(-60, -67.5) * mm, "radius": 4 * mm});
            skCircle(sketch, "E82.1", {"center": v(60, -67.5) * mm, "radius": 4 * mm});
            skCircle(sketch, "E82.2", {"center": v(60, 67.5) * mm, "radius": 4 * mm});
            skCircle(sketch, "E82.3", {"center": v(-60, 67.5) * mm, "radius": 4 * mm});
            skLineSegment(sketch, "E83", {"start": v(0, 90) * mm, "end": v(0, 120) * mm, "construction": true});
            skCircle(sketch, "E84", {"center": v(0, 120) * mm, "radius": 6 * mm});
            skArc(sketch, "E85", {"start": v(15, 120) * mm, "mid": v(0, 135) * mm, "end": v(-15, 120) * mm});
            skLineSegment(sketch, "E86", {"start": v(-15, 108) * mm, "end": v(-33, 90) * mm});
            skLineSegment(sketch, "E87", {"start": v(15, 108) * mm, "end": v(33, 90) * mm});
            skLineSegment(sketch, "E88", {"start": v(-15, 120) * mm, "end": v(-15, 108) * mm});
            skLineSegment(sketch, "E89", {"start": v(15, 120) * mm, "end": v(15, 108) * mm});
            skLineSegment(sketch, "E90", {"start": v(-80, 0) * mm, "end": v(80, 0) * mm, "construction": true});
            skArc(sketch, "E91.MirrorCS", {"start": v(-15, 120) * mm, "mid": v(0, 135) * mm, "end": v(15, 120) * mm});
            skLineSegment(sketch, "E92.MirrorCS", {"start": v(70, 90) * mm, "end": v(-70, 90) * mm});
            skLineSegment(sketch, "E93.MirrorCS", {"start": v(80, 0) * mm, "end": v(-80, 0) * mm, "construction": true});
            skLineSegment(sketch, "E94.MirrorCS", {"start": v(15, -108) * mm, "end": v(33, -90) * mm});
            skLineSegment(sketch, "E95.MirrorCS", {"start": v(15, -120) * mm, "end": v(15, -108) * mm});
            skArc(sketch, "E96.MirrorCS", {"start": v(15, -120) * mm, "mid": v(0, -135) * mm, "end": v(-15, -120) * mm});
            skLineSegment(sketch, "E97.MirrorCS", {"start": v(-15, -120) * mm, "end": v(-15, -108) * mm});
            skLineSegment(sketch, "E98.MirrorCS", {"start": v(-15, -108) * mm, "end": v(-33, -90) * mm});
            skCircle(sketch, "E99.MirrorC", {"center": v(0, -120) * mm, "radius": 6 * mm});
            skLineSegment(sketch, "E100.MirrorCS", {"start": v(0, -90) * mm, "end": v(0, -120) * mm, "construction": true});
            skSolve(sketch);
        }
        {
            var Q0;
            Q0 = qSketchRegion(id + "F16", true);
            var Q1;
            Q1=makeQuery(id+"F2.opExtrude","CAP_FACE",FACE,{"disambiguationData":[OSD([sQuery(id+"F0.wireOp",EDGE,"E12"),sQuery(id+"F0.wireOp",EDGE,"E13"),sQuery(id+"F0.wireOp",EDGE,"E14"),sQuery(id+"F0.wireOp",EDGE,"E15"),sQuery(id+"F0.wireOp",EDGE,"E17.filletArc"),sQuery(id+"F0.wireOp",EDGE,"E18.filletArc"),sQuery(id+"F0.wireOp",EDGE,"E19.filletArc"),sQuery(id+"F0.wireOp",EDGE,"E20.filletArc"),sQuery(id+"F0.wireOp",EDGE,"E25.0"),sQuery(id+"F0.wireOp",EDGE,"E25.1"),sQuery(id+"F0.wireOp",EDGE,"E25.2"),sQuery(id+"F0.wireOp",EDGE,"E25.3"),sQuery(id+"F0.wireOp",EDGE,"E25.4"),sQuery(id+"F0.wireOp",EDGE,"E25.5"),sQuery(id+"F0.wireOp",EDGE,"E25.6"),sQuery(id+"F0.wireOp",EDGE,"E25.7")])],"isStart":false});
            extrude(context, id + "F17", {"entities" : qUnion([Q0]), "endBound" : BoundingType.UP_TO_SURFACE, "endBoundEntityFace" : qUnion([Q1]), "depth" : 3 * mm});
        }
    });
